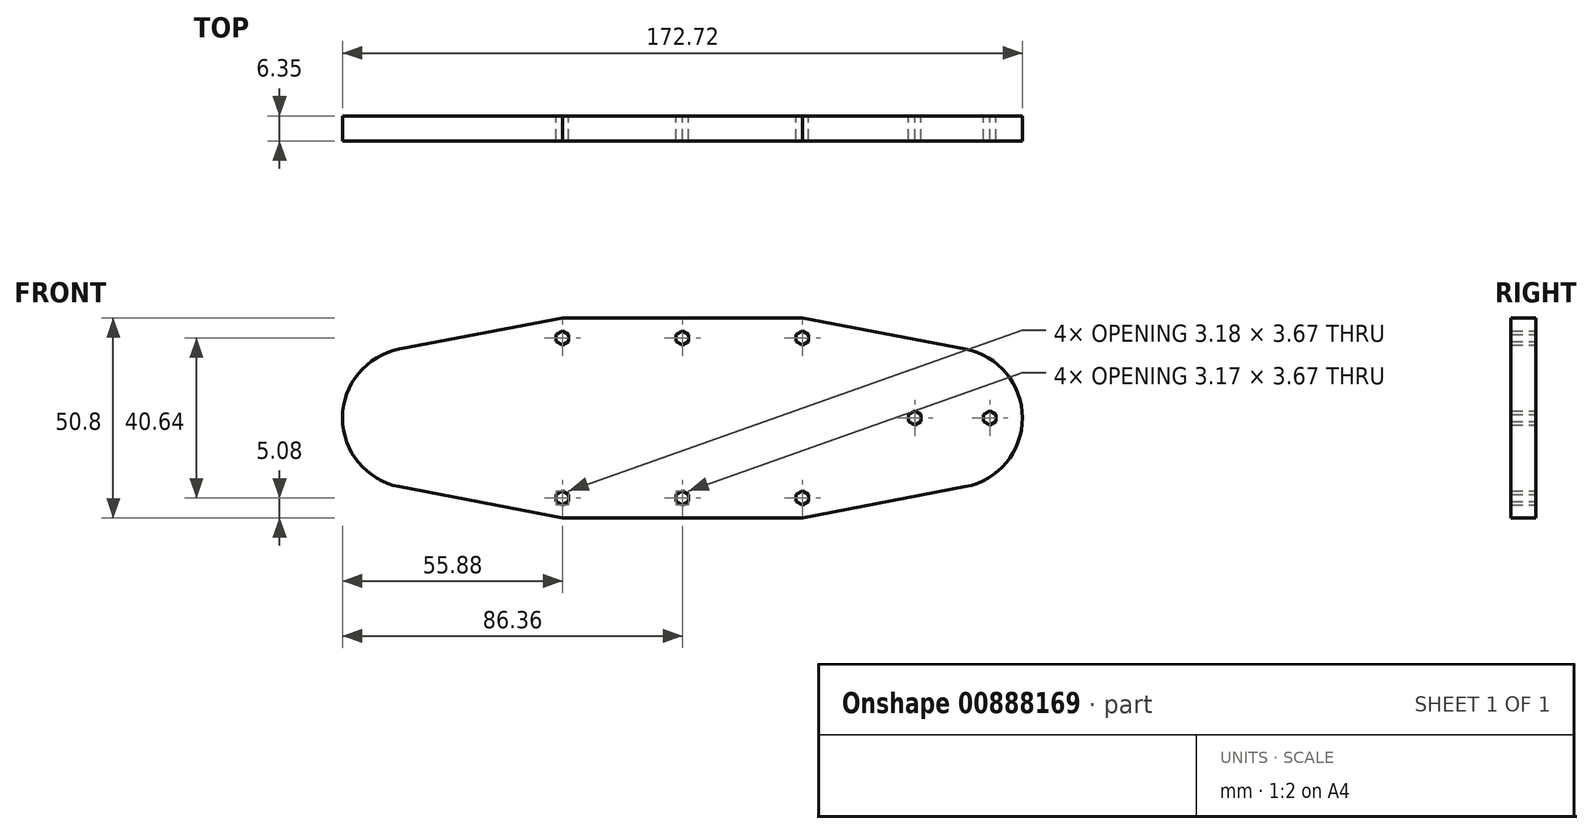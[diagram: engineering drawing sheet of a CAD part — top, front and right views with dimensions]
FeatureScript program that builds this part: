
annotation { "Feature Type Name" : "Feature", "Feature Type Description" : "" }
export const myFeature = defineFeature(function(context is Context, id is Id, definition is map)
    precondition{}
    {
        {
            var Q0;
            Q0=qCreatedBy(makeId("Front.planeOp"),FACE);
            var sketch = newSketch(context, id + "F0", { "sketchPlane" : qUnion([Q0])});
            skLineSegment(sketch, "E0.bottom", {"start": v(68.58, 25.4) * mm, "end": v(-68.58, 25.4) * mm});
            skLineSegment(sketch, "E0.top", {"start": v(68.58, -25.4) * mm, "end": v(-68.58, -25.4) * mm});
            skLineSegment(sketch, "E0.left", {"start": v(68.58, 25.4) * mm, "end": v(68.58, -25.4) * mm});
            skLineSegment(sketch, "E0.right", {"start": v(-68.58, 25.4) * mm, "end": v(-68.58, -25.4) * mm});
            skPoint(sketch, "E0.middle", {"position": v(0, 0) * mm});
            skCircle(sketch, "E1", {"center": v(-68.58, 0) * mm, "radius": 17.78 * mm});
            skCircle(sketch, "E2", {"center": v(68.58, 0) * mm, "radius": 17.78 * mm});
            skLineSegment(sketch, "E3", {"start": v(-30.48, 25.4) * mm, "end": v(-71.92, 17.46) * mm});
            skLineSegment(sketch, "E4", {"start": v(-30.48, -25.4) * mm, "end": v(-71.92, -17.46) * mm});
            skLineSegment(sketch, "E5", {"start": v(30.48, 25.4) * mm, "end": v(71.92, 17.46) * mm});
            skLineSegment(sketch, "E6", {"start": v(30.48, -25.4) * mm, "end": v(71.92, -17.46) * mm});
            skCircle(sketch, "E7.cCircle", {"center": v(59.06, 0) * mm, "radius": 1.59 * mm, "construction": true});
            skLineSegment(sketch, "E7.0", {"start": v(57.47, -0.92) * mm, "end": v(57.47, 0.92) * mm});
            skLineSegment(sketch, "E7.1", {"start": v(57.47, 0.92) * mm, "end": v(59.06, 1.83) * mm});
            skLineSegment(sketch, "E7.2", {"start": v(59.06, 1.83) * mm, "end": v(60.64, 0.92) * mm});
            skLineSegment(sketch, "E7.3", {"start": v(60.64, 0.92) * mm, "end": v(60.64, -0.92) * mm});
            skLineSegment(sketch, "E7.4", {"start": v(60.64, -0.92) * mm, "end": v(59.06, -1.83) * mm});
            skLineSegment(sketch, "E7.5", {"start": v(59.06, -1.83) * mm, "end": v(57.47, -0.92) * mm});
            skPoint(sketch, "E7.0.midPoint", {"position": v(57.47, 0) * mm});
            skCircle(sketch, "E8.cCircle", {"center": v(78.1, 0) * mm, "radius": 1.59 * mm, "construction": true});
            skLineSegment(sketch, "E8.0", {"start": v(79.7, 0.92) * mm, "end": v(79.7, -0.92) * mm});
            skLineSegment(sketch, "E8.1", {"start": v(79.7, -0.92) * mm, "end": v(78.1, -1.83) * mm});
            skLineSegment(sketch, "E8.2", {"start": v(78.1, -1.83) * mm, "end": v(76.52, -0.92) * mm});
            skLineSegment(sketch, "E8.3", {"start": v(76.52, -0.92) * mm, "end": v(76.52, 0.92) * mm});
            skLineSegment(sketch, "E8.4", {"start": v(76.52, 0.92) * mm, "end": v(78.1, 1.83) * mm});
            skLineSegment(sketch, "E8.5", {"start": v(78.1, 1.83) * mm, "end": v(79.7, 0.92) * mm});
            skPoint(sketch, "E8.0.midPoint", {"position": v(79.7, 0) * mm});
            skCircle(sketch, "E9.cCircle", {"center": v(-30.48, 20.32) * mm, "radius": 1.59 * mm, "construction": true});
            skLineSegment(sketch, "E9.0", {"start": v(-28.9, 21.24) * mm, "end": v(-28.9, 19.4) * mm});
            skLineSegment(sketch, "E9.1", {"start": v(-28.9, 19.4) * mm, "end": v(-30.48, 18.49) * mm});
            skLineSegment(sketch, "E9.2", {"start": v(-30.48, 18.49) * mm, "end": v(-32.07, 19.4) * mm});
            skLineSegment(sketch, "E9.3", {"start": v(-32.07, 19.4) * mm, "end": v(-32.07, 21.24) * mm});
            skLineSegment(sketch, "E9.4", {"start": v(-32.07, 21.24) * mm, "end": v(-30.48, 22.15) * mm});
            skLineSegment(sketch, "E9.5", {"start": v(-30.48, 22.15) * mm, "end": v(-28.9, 21.24) * mm});
            skPoint(sketch, "E9.0.midPoint", {"position": v(-28.9, 20.32) * mm});
            skCircle(sketch, "E10.cCircle", {"center": v(0, 20.32) * mm, "radius": 1.59 * mm, "construction": true});
            skLineSegment(sketch, "E10.0", {"start": v(1.59, 21.24) * mm, "end": v(1.59, 19.4) * mm});
            skLineSegment(sketch, "E10.1", {"start": v(1.59, 19.4) * mm, "end": v(0, 18.49) * mm});
            skLineSegment(sketch, "E10.2", {"start": v(0, 18.49) * mm, "end": v(-1.59, 19.4) * mm});
            skLineSegment(sketch, "E10.3", {"start": v(-1.59, 19.4) * mm, "end": v(-1.59, 21.24) * mm});
            skLineSegment(sketch, "E10.4", {"start": v(-1.59, 21.24) * mm, "end": v(0, 22.15) * mm});
            skLineSegment(sketch, "E10.5", {"start": v(0, 22.15) * mm, "end": v(1.59, 21.24) * mm});
            skPoint(sketch, "E10.0.midPoint", {"position": v(1.59, 20.32) * mm});
            skCircle(sketch, "E11.cCircle", {"center": v(30.48, 20.32) * mm, "radius": 1.59 * mm, "construction": true});
            skLineSegment(sketch, "E11.0", {"start": v(28.9, 19.4) * mm, "end": v(28.9, 21.24) * mm});
            skLineSegment(sketch, "E11.1", {"start": v(28.9, 21.24) * mm, "end": v(30.48, 22.15) * mm});
            skLineSegment(sketch, "E11.2", {"start": v(30.48, 22.15) * mm, "end": v(32.07, 21.24) * mm});
            skLineSegment(sketch, "E11.3", {"start": v(32.07, 21.24) * mm, "end": v(32.07, 19.4) * mm});
            skLineSegment(sketch, "E11.4", {"start": v(32.07, 19.4) * mm, "end": v(30.48, 18.49) * mm});
            skLineSegment(sketch, "E11.5", {"start": v(30.48, 18.49) * mm, "end": v(28.9, 19.4) * mm});
            skPoint(sketch, "E11.0.midPoint", {"position": v(28.9, 20.32) * mm});
            skCircle(sketch, "E12.cCircle", {"center": v(-30.48, -20.32) * mm, "radius": 1.59 * mm, "construction": true});
            skLineSegment(sketch, "E12.0", {"start": v(-28.9, -19.4) * mm, "end": v(-28.9, -21.24) * mm});
            skLineSegment(sketch, "E12.1", {"start": v(-28.9, -21.24) * mm, "end": v(-30.48, -22.15) * mm});
            skLineSegment(sketch, "E12.2", {"start": v(-30.48, -22.15) * mm, "end": v(-32.07, -21.24) * mm});
            skLineSegment(sketch, "E12.3", {"start": v(-32.07, -21.24) * mm, "end": v(-32.07, -19.4) * mm});
            skLineSegment(sketch, "E12.4", {"start": v(-32.07, -19.4) * mm, "end": v(-30.48, -18.49) * mm});
            skLineSegment(sketch, "E12.5", {"start": v(-30.48, -18.49) * mm, "end": v(-28.9, -19.4) * mm});
            skPoint(sketch, "E12.0.midPoint", {"position": v(-28.9, -20.32) * mm});
            skCircle(sketch, "E13.cCircle", {"center": v(0, -20.32) * mm, "radius": 1.59 * mm, "construction": true});
            skLineSegment(sketch, "E13.0", {"start": v(1.59, -19.4) * mm, "end": v(1.59, -21.24) * mm});
            skLineSegment(sketch, "E13.1", {"start": v(1.59, -21.24) * mm, "end": v(0, -22.15) * mm});
            skLineSegment(sketch, "E13.2", {"start": v(0, -22.15) * mm, "end": v(-1.59, -21.24) * mm});
            skLineSegment(sketch, "E13.3", {"start": v(-1.59, -21.24) * mm, "end": v(-1.59, -19.4) * mm});
            skLineSegment(sketch, "E13.4", {"start": v(-1.59, -19.4) * mm, "end": v(0, -18.49) * mm});
            skLineSegment(sketch, "E13.5", {"start": v(0, -18.49) * mm, "end": v(1.59, -19.4) * mm});
            skPoint(sketch, "E13.0.midPoint", {"position": v(1.59, -20.32) * mm});
            skCircle(sketch, "E14.cCircle", {"center": v(30.48, -20.32) * mm, "radius": 1.59 * mm, "construction": true});
            skLineSegment(sketch, "E14.0", {"start": v(28.9, -21.24) * mm, "end": v(28.9, -19.4) * mm});
            skLineSegment(sketch, "E14.1", {"start": v(28.9, -19.4) * mm, "end": v(30.48, -18.49) * mm});
            skLineSegment(sketch, "E14.2", {"start": v(30.48, -18.49) * mm, "end": v(32.07, -19.4) * mm});
            skLineSegment(sketch, "E14.3", {"start": v(32.07, -19.4) * mm, "end": v(32.07, -21.24) * mm});
            skLineSegment(sketch, "E14.4", {"start": v(32.07, -21.24) * mm, "end": v(30.48, -22.15) * mm});
            skLineSegment(sketch, "E14.5", {"start": v(30.48, -22.15) * mm, "end": v(28.9, -21.24) * mm});
            skPoint(sketch, "E14.0.midPoint", {"position": v(28.9, -20.32) * mm});
            skCircle(sketch, "E15.cCircle", {"center": v(-68.58, 0) * mm, "radius": 6.35 * mm, "construction": true});
            skLineSegment(sketch, "E15.0", {"start": v(-62.23, 3.67) * mm, "end": v(-62.23, -3.67) * mm});
            skLineSegment(sketch, "E15.1", {"start": v(-62.23, -3.67) * mm, "end": v(-68.58, -7.33) * mm});
            skLineSegment(sketch, "E15.2", {"start": v(-68.58, -7.33) * mm, "end": v(-74.93, -3.67) * mm});
            skLineSegment(sketch, "E15.3", {"start": v(-74.93, -3.67) * mm, "end": v(-74.93, 3.67) * mm});
            skLineSegment(sketch, "E15.4", {"start": v(-74.93, 3.67) * mm, "end": v(-68.58, 7.33) * mm});
            skLineSegment(sketch, "E15.5", {"start": v(-68.58, 7.33) * mm, "end": v(-62.23, 3.67) * mm});
            skPoint(sketch, "E15.0.midPoint", {"position": v(-62.23, 0) * mm});
            skCircle(sketch, "E16", {"center": v(-61.57, 0) * mm, "radius": 15.5 * mm, "construction": true});
            skCircle(sketch, "E17.cCircle", {"center": v(-61.57, 15.5) * mm, "radius": 1.59 * mm, "construction": true});
            skLineSegment(sketch, "E17.0", {"start": v(-59.98, 16.41) * mm, "end": v(-59.98, 14.58) * mm});
            skLineSegment(sketch, "E17.1", {"start": v(-59.98, 14.58) * mm, "end": v(-61.57, 13.66) * mm});
            skLineSegment(sketch, "E17.2", {"start": v(-61.57, 13.66) * mm, "end": v(-63.16, 14.58) * mm});
            skLineSegment(sketch, "E17.3", {"start": v(-63.16, 14.58) * mm, "end": v(-63.16, 16.41) * mm});
            skLineSegment(sketch, "E17.4", {"start": v(-63.16, 16.41) * mm, "end": v(-61.57, 17.33) * mm});
            skLineSegment(sketch, "E17.5", {"start": v(-61.57, 17.33) * mm, "end": v(-59.98, 16.41) * mm});
            skPoint(sketch, "E17.0.midPoint", {"position": v(-59.98, 15.5) * mm});
            skCircle(sketch, "E18.cCircle", {"center": v(-61.57, -15.5) * mm, "radius": 1.59 * mm, "construction": true});
            skLineSegment(sketch, "E18.0", {"start": v(-59.98, -14.58) * mm, "end": v(-59.98, -16.41) * mm});
            skLineSegment(sketch, "E18.1", {"start": v(-59.98, -16.41) * mm, "end": v(-61.57, -17.33) * mm});
            skLineSegment(sketch, "E18.2", {"start": v(-61.57, -17.33) * mm, "end": v(-63.16, -16.41) * mm});
            skLineSegment(sketch, "E18.3", {"start": v(-63.16, -16.41) * mm, "end": v(-63.16, -14.58) * mm});
            skLineSegment(sketch, "E18.4", {"start": v(-63.16, -14.58) * mm, "end": v(-61.57, -13.66) * mm});
            skLineSegment(sketch, "E18.5", {"start": v(-61.57, -13.66) * mm, "end": v(-59.98, -14.58) * mm});
            skPoint(sketch, "E18.0.midPoint", {"position": v(-59.98, -15.5) * mm});
            skCircle(sketch, "E19.cCircle", {"center": v(-74.99, 7.75) * mm, "radius": 1.59 * mm, "construction": true});
            skLineSegment(sketch, "E19.0", {"start": v(-73.4, 8.66) * mm, "end": v(-73.4, 6.83) * mm});
            skLineSegment(sketch, "E19.1", {"start": v(-73.4, 6.83) * mm, "end": v(-74.99, 5.91) * mm});
            skLineSegment(sketch, "E19.2", {"start": v(-74.99, 5.91) * mm, "end": v(-76.58, 6.83) * mm});
            skLineSegment(sketch, "E19.3", {"start": v(-76.58, 6.83) * mm, "end": v(-76.58, 8.66) * mm});
            skLineSegment(sketch, "E19.4", {"start": v(-76.58, 8.66) * mm, "end": v(-74.99, 9.58) * mm});
            skLineSegment(sketch, "E19.5", {"start": v(-74.99, 9.58) * mm, "end": v(-73.4, 8.66) * mm});
            skPoint(sketch, "E19.0.midPoint", {"position": v(-73.4, 7.75) * mm});
            skCircle(sketch, "E20.cCircle", {"center": v(-48.15, 7.75) * mm, "radius": 1.59 * mm, "construction": true});
            skLineSegment(sketch, "E20.0", {"start": v(-46.56, 8.66) * mm, "end": v(-46.56, 6.83) * mm});
            skLineSegment(sketch, "E20.1", {"start": v(-46.56, 6.83) * mm, "end": v(-48.15, 5.91) * mm});
            skLineSegment(sketch, "E20.2", {"start": v(-48.15, 5.91) * mm, "end": v(-49.74, 6.83) * mm});
            skLineSegment(sketch, "E20.3", {"start": v(-49.74, 6.83) * mm, "end": v(-49.74, 8.66) * mm});
            skLineSegment(sketch, "E20.4", {"start": v(-49.74, 8.66) * mm, "end": v(-48.15, 9.58) * mm});
            skLineSegment(sketch, "E20.5", {"start": v(-48.15, 9.58) * mm, "end": v(-46.56, 8.66) * mm});
            skPoint(sketch, "E20.0.midPoint", {"position": v(-46.56, 7.75) * mm});
            skCircle(sketch, "E21.cCircle", {"center": v(-74.99, -7.75) * mm, "radius": 1.59 * mm, "construction": true});
            skLineSegment(sketch, "E21.0", {"start": v(-76.58, -8.66) * mm, "end": v(-76.58, -6.83) * mm});
            skLineSegment(sketch, "E21.1", {"start": v(-76.58, -6.83) * mm, "end": v(-74.99, -5.91) * mm});
            skLineSegment(sketch, "E21.2", {"start": v(-74.99, -5.91) * mm, "end": v(-73.4, -6.83) * mm});
            skLineSegment(sketch, "E21.3", {"start": v(-73.4, -6.83) * mm, "end": v(-73.4, -8.66) * mm});
            skLineSegment(sketch, "E21.4", {"start": v(-73.4, -8.66) * mm, "end": v(-74.99, -9.58) * mm});
            skLineSegment(sketch, "E21.5", {"start": v(-74.99, -9.58) * mm, "end": v(-76.58, -8.66) * mm});
            skPoint(sketch, "E21.0.midPoint", {"position": v(-76.58, -7.75) * mm});
            skCircle(sketch, "E22.cCircle", {"center": v(-48.15, -7.75) * mm, "radius": 1.59 * mm, "construction": true});
            skLineSegment(sketch, "E22.0", {"start": v(-46.56, -6.83) * mm, "end": v(-46.56, -8.66) * mm});
            skLineSegment(sketch, "E22.1", {"start": v(-46.56, -8.66) * mm, "end": v(-48.15, -9.58) * mm});
            skLineSegment(sketch, "E22.2", {"start": v(-48.15, -9.58) * mm, "end": v(-49.74, -8.66) * mm});
            skLineSegment(sketch, "E22.3", {"start": v(-49.74, -8.66) * mm, "end": v(-49.74, -6.83) * mm});
            skLineSegment(sketch, "E22.4", {"start": v(-49.74, -6.83) * mm, "end": v(-48.15, -5.91) * mm});
            skLineSegment(sketch, "E22.5", {"start": v(-48.15, -5.91) * mm, "end": v(-46.56, -6.83) * mm});
            skPoint(sketch, "E22.0.midPoint", {"position": v(-46.56, -7.75) * mm});
            skLineSegment(sketch, "E23", {"start": v(-68.58, 0) * mm, "end": v(-32.25, 0) * mm, "construction": true});
            skLineSegment(sketch, "E24", {"start": v(-48.15, 7.75) * mm, "end": v(-61.57, 0) * mm, "construction": true});
            skLineSegment(sketch, "E25", {"start": v(-61.57, 0) * mm, "end": v(-48.15, -7.75) * mm, "construction": true});
            skLineSegment(sketch, "E26", {"start": v(-61.57, 0) * mm, "end": v(-74.99, -7.75) * mm, "construction": true});
            skLineSegment(sketch, "E27", {"start": v(-61.57, 0) * mm, "end": v(-74.99, 7.75) * mm, "construction": true});
            skCircle(sketch, "E28.cCircle", {"center": v(-19.05, 17.78) * mm, "radius": 1.59 * mm, "construction": true});
            skLineSegment(sketch, "E28.0", {"start": v(-17.46, 18.7) * mm, "end": v(-17.46, 16.86) * mm});
            skLineSegment(sketch, "E28.1", {"start": v(-17.46, 16.86) * mm, "end": v(-19.05, 15.95) * mm});
            skLineSegment(sketch, "E28.2", {"start": v(-19.05, 15.95) * mm, "end": v(-20.64, 16.86) * mm});
            skLineSegment(sketch, "E28.3", {"start": v(-20.64, 16.86) * mm, "end": v(-20.64, 18.7) * mm});
            skLineSegment(sketch, "E28.4", {"start": v(-20.64, 18.7) * mm, "end": v(-19.05, 19.61) * mm});
            skLineSegment(sketch, "E28.5", {"start": v(-19.05, 19.61) * mm, "end": v(-17.46, 18.7) * mm});
            skPoint(sketch, "E28.0.midPoint", {"position": v(-17.46, 17.78) * mm});
            skCircle(sketch, "E29.cCircle", {"center": v(19.05, 17.78) * mm, "radius": 1.59 * mm, "construction": true});
            skLineSegment(sketch, "E29.0", {"start": v(20.64, 18.7) * mm, "end": v(20.64, 16.86) * mm});
            skLineSegment(sketch, "E29.1", {"start": v(20.64, 16.86) * mm, "end": v(19.05, 15.95) * mm});
            skLineSegment(sketch, "E29.2", {"start": v(19.05, 15.95) * mm, "end": v(17.46, 16.86) * mm});
            skLineSegment(sketch, "E29.3", {"start": v(17.46, 16.86) * mm, "end": v(17.46, 18.7) * mm});
            skLineSegment(sketch, "E29.4", {"start": v(17.46, 18.7) * mm, "end": v(19.05, 19.61) * mm});
            skLineSegment(sketch, "E29.5", {"start": v(19.05, 19.61) * mm, "end": v(20.64, 18.7) * mm});
            skPoint(sketch, "E29.0.midPoint", {"position": v(20.64, 17.78) * mm});
            skCircle(sketch, "E30.cCircle", {"center": v(-19.05, -17.78) * mm, "radius": 1.59 * mm, "construction": true});
            skLineSegment(sketch, "E30.0", {"start": v(-17.46, -16.86) * mm, "end": v(-17.46, -18.7) * mm});
            skLineSegment(sketch, "E30.1", {"start": v(-17.46, -18.7) * mm, "end": v(-19.05, -19.61) * mm});
            skLineSegment(sketch, "E30.2", {"start": v(-19.05, -19.61) * mm, "end": v(-20.64, -18.7) * mm});
            skLineSegment(sketch, "E30.3", {"start": v(-20.64, -18.7) * mm, "end": v(-20.64, -16.86) * mm});
            skLineSegment(sketch, "E30.4", {"start": v(-20.64, -16.86) * mm, "end": v(-19.05, -15.95) * mm});
            skLineSegment(sketch, "E30.5", {"start": v(-19.05, -15.95) * mm, "end": v(-17.46, -16.86) * mm});
            skPoint(sketch, "E30.0.midPoint", {"position": v(-17.46, -17.78) * mm});
            skCircle(sketch, "E31.cCircle", {"center": v(19.05, -17.78) * mm, "radius": 1.59 * mm, "construction": true});
            skLineSegment(sketch, "E31.0", {"start": v(17.46, -18.7) * mm, "end": v(17.46, -16.86) * mm});
            skLineSegment(sketch, "E31.1", {"start": v(17.46, -16.86) * mm, "end": v(19.05, -15.95) * mm});
            skLineSegment(sketch, "E31.2", {"start": v(19.05, -15.95) * mm, "end": v(20.64, -16.86) * mm});
            skLineSegment(sketch, "E31.3", {"start": v(20.64, -16.86) * mm, "end": v(20.64, -18.7) * mm});
            skLineSegment(sketch, "E31.4", {"start": v(20.64, -18.7) * mm, "end": v(19.05, -19.61) * mm});
            skLineSegment(sketch, "E31.5", {"start": v(19.05, -19.61) * mm, "end": v(17.46, -18.7) * mm});
            skPoint(sketch, "E31.0.midPoint", {"position": v(17.46, -17.78) * mm});
            skSolve(sketch);
        }
        {
            var Q0;
            Q0=makeQuery(id+"F0.imprint","IMPRINT",FACE,{"disambiguationData":[TD([[makeQuery(id+"F0.imprint","IMPRINT",EDGE,{"derivedFrom":sQuery(id+"F0.wireOp",EDGE,"E9.0")}),1.0]])]});
            var Q1;
            Q1=makeQuery(id+"F0.imprint","IMPRINT",FACE,{"disambiguationData":[TD([[makeQuery(id+"F0.imprint","IMPRINT",EDGE,{"derivedFrom":sQuery(id+"F0.wireOp",EDGE,"E15.0")}),1.0]])]});
            var Q2;
            {var subQ4=sQuery(id+"F0.wireOp",EDGE,"E15.2");Q2=makeQuery(id+"F0.imprint","IMPRINT",FACE,{"disambiguationData":[TD([[makeQuery(id+"F0.imprint","IMPRINT",EDGE,{"derivedFrom":subQ4}),1.0]])]});}
            var Q3;
            Q3=makeQuery(id+"F0.imprint","IMPRINT",FACE,{"disambiguationData":[TD([[makeQuery(id+"F0.imprint","IMPRINT",EDGE,{"derivedFrom":sQuery(id+"F0.wireOp",EDGE,"E7.0")}),1.0]])]});
            var Q4;
            Q4=makeQuery(id+"F0.imprint","IMPRINT",FACE,{"disambiguationData":[TD([[makeQuery(id+"F0.imprint","IMPRINT",EDGE,{"derivedFrom":sQuery(id+"F0.wireOp",EDGE,"E8.0")}),1.0]])]});
            var Q5;
            {var subQ0=sQuery(id+"F0.wireOp",EDGE,"E4");var subQ1=sQuery(id+"F0.wireOp",EDGE,"E0.right");var subQ2=makeQuery(id+"F0.imprint","INTERSECT",VERTEX,{"derivedFrom":[subQ1,subQ0]});Q5=makeQuery(id+"F0.imprint","IMPRINT",FACE,{"disambiguationData":[TD([[makeQuery(id+"F0.imprint","IMPRINT",EDGE,{"disambiguationData":[TD([[subQ2,1.0]])],"derivedFrom":subQ1}),-1.0]])]});}
            var Q6;
            {var subQ0=sQuery(id+"F0.wireOp",EDGE,"E3");var subQ1=sQuery(id+"F0.wireOp",EDGE,"E0.right");var subQ2=makeQuery(id+"F0.imprint","INTERSECT",VERTEX,{"derivedFrom":[subQ1,subQ0]});Q6=makeQuery(id+"F0.imprint","IMPRINT",FACE,{"disambiguationData":[TD([[makeQuery(id+"F0.imprint","IMPRINT",EDGE,{"disambiguationData":[TD([[subQ2,-1.0]])],"derivedFrom":subQ1}),-1.0]])]});}
            var Q7;
            {var subQ0=sQuery(id+"F0.wireOp",EDGE,"E5");var subQ1=sQuery(id+"F0.wireOp",EDGE,"E0.left");var subQ2=makeQuery(id+"F0.imprint","INTERSECT",VERTEX,{"derivedFrom":[subQ1,subQ0]});Q7=makeQuery(id+"F0.imprint","IMPRINT",FACE,{"disambiguationData":[TD([[makeQuery(id+"F0.imprint","IMPRINT",EDGE,{"disambiguationData":[TD([[subQ2,-1.0]])],"derivedFrom":subQ1}),1.0]])]});}
            var Q8;
            {var subQ0=sQuery(id+"F0.wireOp",EDGE,"E6");var subQ1=sQuery(id+"F0.wireOp",EDGE,"E0.left");var subQ2=makeQuery(id+"F0.imprint","INTERSECT",VERTEX,{"derivedFrom":[subQ1,subQ0]});Q8=makeQuery(id+"F0.imprint","IMPRINT",FACE,{"disambiguationData":[TD([[makeQuery(id+"F0.imprint","IMPRINT",EDGE,{"disambiguationData":[TD([[subQ2,1.0]])],"derivedFrom":subQ1}),1.0]])]});}
            var Q9;
            Q9=makeQuery(id+"F0.imprint","IMPRINT",FACE,{"disambiguationData":[TD([[makeQuery(id+"F0.imprint","IMPRINT",EDGE,{"derivedFrom":sQuery(id+"F0.wireOp",EDGE,"E19.0")}),-1.0]])]});
            var Q10;
            Q10=makeQuery(id+"F0.imprint","IMPRINT",FACE,{"disambiguationData":[TD([[makeQuery(id+"F0.imprint","IMPRINT",EDGE,{"derivedFrom":sQuery(id+"F0.wireOp",EDGE,"E21.0")}),-1.0]])]});
            var Q11;
            {var subQ0=sQuery(id+"F0.wireOp",EDGE,"E15.2");Q11=makeQuery(id+"F0.imprint","IMPRINT",FACE,{"disambiguationData":[TD([[makeQuery(id+"F0.imprint","IMPRINT",EDGE,{"derivedFrom":subQ0}),-1.0]])]});}
            var Q12;
            Q12=makeQuery(id+"F0.imprint","IMPRINT",FACE,{"disambiguationData":[TD([[makeQuery(id+"F0.imprint","IMPRINT",EDGE,{"derivedFrom":sQuery(id+"F0.wireOp",EDGE,"E15.0")}),-1.0]])]});
            var Q13;
            {var subQ5=sQuery(id+"F0.wireOp",EDGE,"E17.1");Q13=makeQuery(id+"F0.imprint","IMPRINT",FACE,{"disambiguationData":[TD([[makeQuery(id+"F0.imprint","IMPRINT",EDGE,{"derivedFrom":subQ5}),-1.0]])]});}
            var Q14;
            {var subQ5=sQuery(id+"F0.wireOp",EDGE,"E17.5");Q14=makeQuery(id+"F0.imprint","IMPRINT",FACE,{"disambiguationData":[TD([[makeQuery(id+"F0.imprint","IMPRINT",EDGE,{"derivedFrom":subQ5}),-1.0]])]});}
            var Q15;
            Q15=makeQuery(id+"F0.imprint","IMPRINT",FACE,{"disambiguationData":[TD([[makeQuery(id+"F0.imprint","IMPRINT",EDGE,{"derivedFrom":sQuery(id+"F0.wireOp",EDGE,"E20.0")}),-1.0]])]});
            var Q16;
            Q16=makeQuery(id+"F0.imprint","IMPRINT",FACE,{"disambiguationData":[TD([[makeQuery(id+"F0.imprint","IMPRINT",EDGE,{"derivedFrom":sQuery(id+"F0.wireOp",EDGE,"E22.0")}),-1.0]])]});
            var Q17;
            {var subQ0=sQuery(id+"F0.wireOp",EDGE,"E18.3");Q17=makeQuery(id+"F0.imprint","IMPRINT",FACE,{"disambiguationData":[TD([[makeQuery(id+"F0.imprint","IMPRINT",EDGE,{"derivedFrom":subQ0}),-1.0]])]});}
            var Q18;
            {var subQ5=sQuery(id+"F0.wireOp",EDGE,"E18.1");Q18=makeQuery(id+"F0.imprint","IMPRINT",FACE,{"disambiguationData":[TD([[makeQuery(id+"F0.imprint","IMPRINT",EDGE,{"derivedFrom":subQ5}),-1.0]])]});}
            var Q19;
            Q19=makeQuery(id+"F0.imprint","IMPRINT",FACE,{"disambiguationData":[TD([[makeQuery(id+"F0.imprint","IMPRINT",EDGE,{"derivedFrom":sQuery(id+"F0.wireOp",EDGE,"E28.0")}),-1.0]])]});
            var Q20;
            Q20=makeQuery(id+"F0.imprint","IMPRINT",FACE,{"disambiguationData":[TD([[makeQuery(id+"F0.imprint","IMPRINT",EDGE,{"derivedFrom":sQuery(id+"F0.wireOp",EDGE,"E30.0")}),-1.0]])]});
            var Q21;
            Q21=makeQuery(id+"F0.imprint","IMPRINT",FACE,{"disambiguationData":[TD([[makeQuery(id+"F0.imprint","IMPRINT",EDGE,{"derivedFrom":sQuery(id+"F0.wireOp",EDGE,"E31.0")}),-1.0]])]});
            var Q22;
            Q22=makeQuery(id+"F0.imprint","IMPRINT",FACE,{"disambiguationData":[TD([[makeQuery(id+"F0.imprint","IMPRINT",EDGE,{"derivedFrom":sQuery(id+"F0.wireOp",EDGE,"E29.0")}),-1.0]])]});
            extrude(context, id + "F1", {"entities" : qUnion([Q0, Q1, Q2, Q3, Q4, Q5, Q6, Q7, Q8, Q9, Q10, Q11, Q12, Q13, Q14, Q15, Q16, Q17, Q18, Q19, Q20, Q21, Q22]), "depth" : 6.35 * mm, "offsetDistance" : 25.4 * mm});
        }
    });
